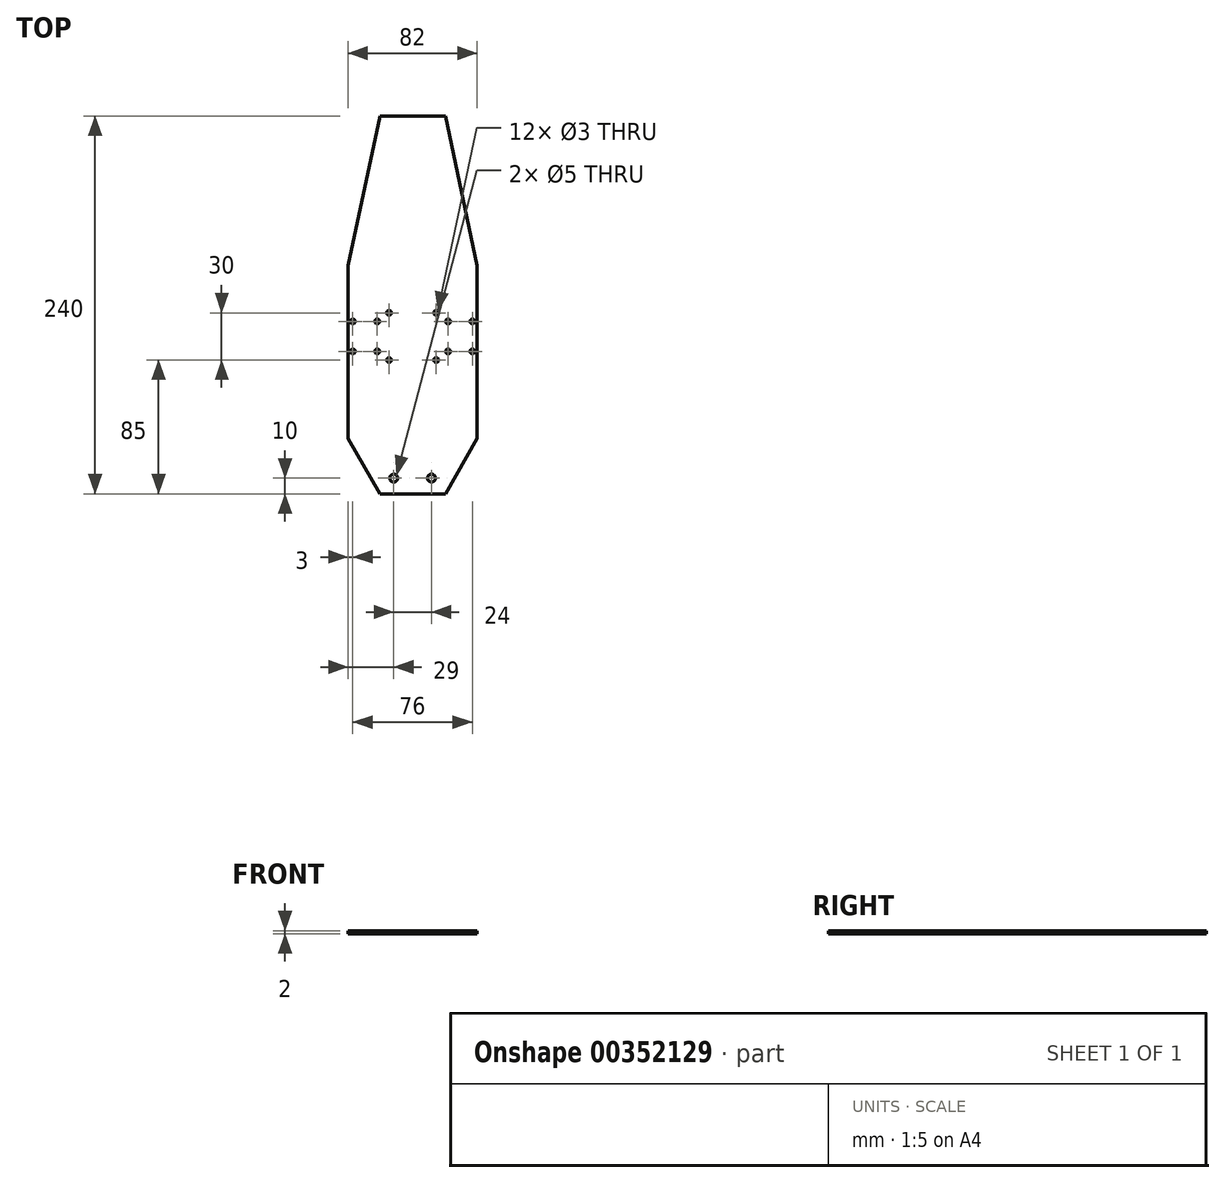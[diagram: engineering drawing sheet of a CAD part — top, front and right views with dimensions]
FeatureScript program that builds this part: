
annotation { "Feature Type Name" : "Feature", "Feature Type Description" : "" }
export const myFeature = defineFeature(function(context is Context, id is Id, definition is map)
    precondition{}
    {
        {
            var Q0;
            Q0=qCreatedBy(makeId("Top.planeOp"),FACE);
            var sketch = newSketch(context, id + "F0", { "sketchPlane" : qUnion([Q0])});
            skLineSegment(sketch, "E0.bottom", {"start": v(0, 0) * mm, "end": v(82, 0) * mm});
            skLineSegment(sketch, "E0.top", {"start": v(0, 110) * mm, "end": v(82, 110) * mm});
            skLineSegment(sketch, "E0.left", {"start": v(0, 0) * mm, "end": v(0, 110) * mm});
            skLineSegment(sketch, "E0.right", {"start": v(82, 0) * mm, "end": v(82, 110) * mm});
            skLineSegment(sketch, "E1", {"start": v(41, 110) * mm, "end": v(41, 0) * mm, "construction": true});
            skLineSegment(sketch, "E2", {"start": v(0, 0) * mm, "end": v(20.19, -35) * mm});
            skLineSegment(sketch, "E3", {"start": v(20.19, -35) * mm, "end": v(61.81, -35) * mm});
            skLineSegment(sketch, "E4", {"start": v(61.81, -35) * mm, "end": v(82, 0) * mm});
            skLineSegment(sketch, "E5", {"start": v(0, 110) * mm, "end": v(20.19, 205) * mm});
            skLineSegment(sketch, "E6", {"start": v(20.19, 205) * mm, "end": v(61.81, 205) * mm});
            skLineSegment(sketch, "E7", {"start": v(61.81, 205) * mm, "end": v(82, 110) * mm});
            skSolve(sketch);
        }
        {
            var Q0;
            Q0=makeQuery(id+"F0.imprint","IMPRINT",FACE,{"disambiguationData":[TD([[makeQuery(id+"F0.imprint","IMPRINT",EDGE,{"derivedFrom":sQuery(id+"F0.wireOp",EDGE,"E0.top")}),1.0]])]});
            var Q1;
            Q1=makeQuery(id+"F0.imprint","IMPRINT",FACE,{"disambiguationData":[TD([[makeQuery(id+"F0.imprint","IMPRINT",EDGE,{"derivedFrom":sQuery(id+"F0.wireOp",EDGE,"E0.bottom")}),1.0]])]});
            var Q2;
            Q2=makeQuery(id+"F0.imprint","IMPRINT",FACE,{"disambiguationData":[TD([[makeQuery(id+"F0.imprint","IMPRINT",EDGE,{"derivedFrom":sQuery(id+"F0.wireOp",EDGE,"E0.bottom")}),-1.0]])]});
            extrude(context, id + "F1", {"entities" : qUnion([Q0, Q1, Q2]), "depth" : 2 * mm});
        }
        {
            var Q0;
            Q0=makeQuery(id+"F1.opExtrude","CAP_FACE",FACE,{"disambiguationData":[OSD([sQuery(id+"F0.wireOp",EDGE,"E0.left"),sQuery(id+"F0.wireOp",EDGE,"E0.right"),sQuery(id+"F0.wireOp",EDGE,"E2"),sQuery(id+"F0.wireOp",EDGE,"E3"),sQuery(id+"F0.wireOp",EDGE,"E4"),sQuery(id+"F0.wireOp",EDGE,"E5"),sQuery(id+"F0.wireOp",EDGE,"E6"),sQuery(id+"F0.wireOp",EDGE,"E7")])],"isStart":false});
            var sketch = newSketch(context, id + "F2", { "sketchPlane" : qUnion([Q0])});
            skPoint(sketch, "E8", {"position": v(3, 74.5) * mm});
            skPoint(sketch, "E9", {"position": v(3, 55.5) * mm});
            skPoint(sketch, "E10", {"position": v(18.5, 74.5) * mm});
            skPoint(sketch, "E11", {"position": v(18.5, 55.5) * mm});
            skPoint(sketch, "E12", {"position": v(63.5, 74.5) * mm});
            skPoint(sketch, "E13", {"position": v(79, 74.5) * mm});
            skPoint(sketch, "E14", {"position": v(63.5, 55.5) * mm});
            skPoint(sketch, "E15", {"position": v(79, 55.5) * mm});
            skLineSegment(sketch, "E16", {"start": v(3, 74.5) * mm, "end": v(3, 55.5) * mm, "construction": true});
            skLineSegment(sketch, "E17", {"start": v(18.5, 74.5) * mm, "end": v(18.5, 55.5) * mm, "construction": true});
            skLineSegment(sketch, "E18", {"start": v(63.5, 74.5) * mm, "end": v(63.5, 55.5) * mm, "construction": true});
            skLineSegment(sketch, "E19", {"start": v(79, 74.5) * mm, "end": v(79, 55.5) * mm, "construction": true});
            skLineSegment(sketch, "E20", {"start": v(4.02, 65) * mm, "end": v(76.96, 65) * mm, "construction": true});
            skLineSegment(sketch, "E21", {"start": v(41, 205) * mm, "end": v(41, -35) * mm, "construction": true});
            skSolve(sketch);
        }
        {
            var Q0;
            Q0=sQuery(id+"F2.wireOp",VERTEX,"E11");
            var Q1;
            Q1=sQuery(id+"F2.wireOp",VERTEX,"E9");
            var Q2;
            Q2=sQuery(id+"F2.wireOp",VERTEX,"E8");
            var Q3;
            Q3=sQuery(id+"F2.wireOp",VERTEX,"E10");
            var Q4;
            Q4=sQuery(id+"F2.wireOp",VERTEX,"E12");
            var Q5;
            Q5=sQuery(id+"F2.wireOp",VERTEX,"E14");
            var Q6;
            Q6=sQuery(id+"F2.wireOp",VERTEX,"E15");
            var Q7;
            Q7=sQuery(id+"F2.wireOp",VERTEX,"E13");
            var Q8;
            Q8=makeQuery(id+"F1.opExtrude","SWEPT_BODY",BODY,{"disambiguationData":[OSD([sQuery(id+"F0.wireOp",EDGE,"E0.left"),sQuery(id+"F0.wireOp",EDGE,"E0.right"),sQuery(id+"F0.wireOp",EDGE,"E2"),sQuery(id+"F0.wireOp",EDGE,"E3"),sQuery(id+"F0.wireOp",EDGE,"E4"),sQuery(id+"F0.wireOp",EDGE,"E5"),sQuery(id+"F0.wireOp",EDGE,"E6"),sQuery(id+"F0.wireOp",EDGE,"E7")])]});
            hole(context, id + "F3", {"style" : HoleStyle.SIMPLE, "endStyle" : HoleEndStyle.THROUGH, "standardTappedOrClearance" : lookupTablePath({ "standard" : "Benutzerdefiniert" }), "standardBlindInLast" : lookupTablePath({ "standard" : "Benutzerdefiniert" }), "holeDiameter" : 3 * mm, "isTappedThrough" : true, "tappedDepth" : 12 * mm, "tapClearance" : 3, "locations" : qUnion([Q0, Q1, Q2, Q3, Q4, Q5, Q6, Q7]), "scope" : qUnion([Q8])});
        }
        {
            var Q0;
            Q0=makeQuery(id+"F1.opExtrude","CAP_FACE",FACE,{"disambiguationData":[OSD([sQuery(id+"F0.wireOp",EDGE,"E0.left"),sQuery(id+"F0.wireOp",EDGE,"E0.right"),sQuery(id+"F0.wireOp",EDGE,"E2"),sQuery(id+"F0.wireOp",EDGE,"E3"),sQuery(id+"F0.wireOp",EDGE,"E4"),sQuery(id+"F0.wireOp",EDGE,"E5"),sQuery(id+"F0.wireOp",EDGE,"E6"),sQuery(id+"F0.wireOp",EDGE,"E7")])],"isStart":false});
            var sketch = newSketch(context, id + "F4", { "sketchPlane" : qUnion([Q0])});
            skPoint(sketch, "E22", {"position": v(29, -25) * mm});
            skPoint(sketch, "E23", {"position": v(53, -25) * mm});
            skLineSegment(sketch, "E24", {"start": v(20.55, -25) * mm, "end": v(67.85, -25) * mm, "construction": true});
            skLineSegment(sketch, "E25", {"start": v(41, -35) * mm, "end": v(41, 205) * mm, "construction": true});
            skSolve(sketch);
        }
        {
            var Q0;
            Q0=sQuery(id+"F4.wireOp",VERTEX,"E22");
            var Q1;
            Q1=sQuery(id+"F4.wireOp",VERTEX,"E23");
            var Q2;
            Q2=makeQuery(id+"F1.opExtrude","SWEPT_BODY",BODY,{"disambiguationData":[OSD([sQuery(id+"F0.wireOp",EDGE,"E0.left"),sQuery(id+"F0.wireOp",EDGE,"E0.right"),sQuery(id+"F0.wireOp",EDGE,"E2"),sQuery(id+"F0.wireOp",EDGE,"E3"),sQuery(id+"F0.wireOp",EDGE,"E4"),sQuery(id+"F0.wireOp",EDGE,"E5"),sQuery(id+"F0.wireOp",EDGE,"E6"),sQuery(id+"F0.wireOp",EDGE,"E7")])]});
            hole(context, id + "F5", {"style" : HoleStyle.SIMPLE, "endStyle" : HoleEndStyle.THROUGH, "holeDiameter" : 5 * mm, "isTappedThrough" : true, "tappedDepth" : 12 * mm, "tapClearance" : 3, "locations" : qUnion([Q0, Q1]), "scope" : qUnion([Q2])});
        }
        {
            var Q0;
            Q0=makeQuery(id+"F1.opExtrude","CAP_FACE",FACE,{"disambiguationData":[OSD([sQuery(id+"F0.wireOp",EDGE,"E0.left"),sQuery(id+"F0.wireOp",EDGE,"E0.right"),sQuery(id+"F0.wireOp",EDGE,"E2"),sQuery(id+"F0.wireOp",EDGE,"E3"),sQuery(id+"F0.wireOp",EDGE,"E4"),sQuery(id+"F0.wireOp",EDGE,"E5"),sQuery(id+"F0.wireOp",EDGE,"E6"),sQuery(id+"F0.wireOp",EDGE,"E7")])],"isStart":false});
            var sketch = newSketch(context, id + "F6", { "sketchPlane" : qUnion([Q0])});
            skPoint(sketch, "E26", {"position": v(26, 50) * mm});
            skPoint(sketch, "E27", {"position": v(26, 80) * mm});
            skPoint(sketch, "E28", {"position": v(56, 50) * mm});
            skPoint(sketch, "E29", {"position": v(56, 80) * mm});
            skLineSegment(sketch, "E30", {"start": v(26, 80) * mm, "end": v(26, 50) * mm, "construction": true});
            skLineSegment(sketch, "E31", {"start": v(56, 80) * mm, "end": v(26, 80) * mm, "construction": true});
            skLineSegment(sketch, "E32", {"start": v(56, 50) * mm, "end": v(26, 50) * mm, "construction": true});
            skLineSegment(sketch, "E33", {"start": v(56, 50) * mm, "end": v(56, 80) * mm, "construction": true});
            skLineSegment(sketch, "E34", {"start": v(41, -35) * mm, "end": v(41, 205) * mm, "construction": true});
            skSolve(sketch);
        }
        {
            var Q0;
            Q0=sQuery(id+"F6.wireOp",VERTEX,"E27");
            var Q1;
            Q1=sQuery(id+"F6.wireOp",VERTEX,"E28");
            var Q2;
            Q2=sQuery(id+"F6.wireOp",VERTEX,"E29");
            var Q3;
            Q3=sQuery(id+"F6.wireOp",VERTEX,"E26");
            var Q4;
            Q4=makeQuery(id+"F1.opExtrude","SWEPT_BODY",BODY,{"disambiguationData":[OSD([sQuery(id+"F0.wireOp",EDGE,"E0.left"),sQuery(id+"F0.wireOp",EDGE,"E0.right"),sQuery(id+"F0.wireOp",EDGE,"E2"),sQuery(id+"F0.wireOp",EDGE,"E3"),sQuery(id+"F0.wireOp",EDGE,"E4"),sQuery(id+"F0.wireOp",EDGE,"E5"),sQuery(id+"F0.wireOp",EDGE,"E6"),sQuery(id+"F0.wireOp",EDGE,"E7")])]});
            hole(context, id + "F7", {"style" : HoleStyle.SIMPLE, "endStyle" : HoleEndStyle.THROUGH, "holeDiameter" : 3 * mm, "isTappedThrough" : true, "tappedDepth" : 12 * mm, "tapClearance" : 3, "locations" : qUnion([Q0, Q1, Q2, Q3]), "scope" : qUnion([Q4])});
        }
    });
